# Revit family: Shower-Showerhead-KOHLER-Purist-K-22170
name_source: partatom
category: Plumbing Fixtures
revit_build: Autodesk Revit 2015 (Build: 20140606_1530(x64)
units: mm (PartAtom-declared; Revit-internal decimal feet)

## types (12) — shared parameters
ADA Compliant = No
Assembly Code = D2010700
CW Connection = No
Cold Water Inlet = Cold Water Inlet
Date Modified = 10/23/2018
Default Elevation = 0"
Description = Multi-function Showerhead
Drain Included = No
HW Connection = Yes
Height = 5 1/2"
Length = 4 5/16"
Manufacturer = KOHLER Co.
MasterFormat 1995 = 15410
MasterFormat 2004 = 22.41.23
Material = Premium Metal Construction
Pressure = 0.00 psi
Product Documentation Link = http://www.us.kohler.com
Product Name = Purist
Product Page URL = http://www.us.kohler.com
Tempered Water Inlet = Tempered Water Inlet
URL = https://www.us.kohler.com
Vent Connection = No
Waste Connection = No
Waste Water Outlet = Waste Water Outlet
Width = 5 1/2"

## per-type parameters (varying)
| type | 1.75 GPM | 2.5 GPM | Finish | Flow Rate | Model | Type |
| 2.5 gpm, CP-Polished Chrome | No | Yes | Kohler-Metal-CP-Polished_Chrome | 3 GPM | K-22170-CP | 1 |
| 2.5 gpm, SN-Vibrant Polished Nickel | No | Yes | Kohler-Metal-SN-Vibrant_Polished_Nickel | 3 GPM | K-22170-SN | 2 |
| 2.5 gpm, BN-Vibrant Brushed Nickel | No | Yes | Kohler-Metal-BN-Vibrant_Brushed_Nickel | 3 GPM | K-22170-BN | 3 |
| 2.5 gpm, BV-Vibrant Brushed Bronze | No | Yes | Kohler-Metal-BV-Brushed_Bronze | 3 GPM | K-22170-BV | 4 |
| 2.5 gpm, RGD-Vibrant Rose Gold | No | Yes | Kohler-Metal-RGD-Polished_Rose_Gold | 3 GPM | K-22170-RGD | 5 |
| 2.5 gpm, TT-Titanium | No | Yes | Kohler-Metal-TT-Vibrant_Titanium | 3 GPM | K-22170-TT | 6 |
| 1.75 gpm, CP-Polished Chrome | Yes | No | Kohler-Metal-CP-Polished_Chrome | 2 GPM | K-22170-G-CP | 7 |
| 1.75 gpm, SN-Vibrant Polished Nickel | Yes | No | Kohler-Metal-SN-Vibrant_Polished_Nickel | 2 GPM | K-22170-G-SN | 8 |
| 1.75 gpm, BN-Vibrant Brushed Nickel | Yes | No | Kohler-Metal-BN-Vibrant_Brushed_Nickel | 2 GPM | K-22170-G-BN | 9 |
| 1.75 gpm, BV-Vibrant Brushed Bronze | Yes | No | Kohler-Metal-BV-Brushed_Bronze | 2 GPM | K-22170-G-BV | 10 |
| 1.75 gpm, RGD-Vibrant Rose Gold | Yes | No | Kohler-Metal-RGD-Polished_Rose_Gold | 2 GPM | K-22170-G-RGD | 11 |
| 1.75 gpm, TT-Titanium | Yes | No | Kohler-Metal-TT-Vibrant_Titanium | 2 GPM | K-22170-G-TT | 12 |

## geometry (parser evidence)
native form markers: Sweep x5
no freeform markers — native parametric forms only
